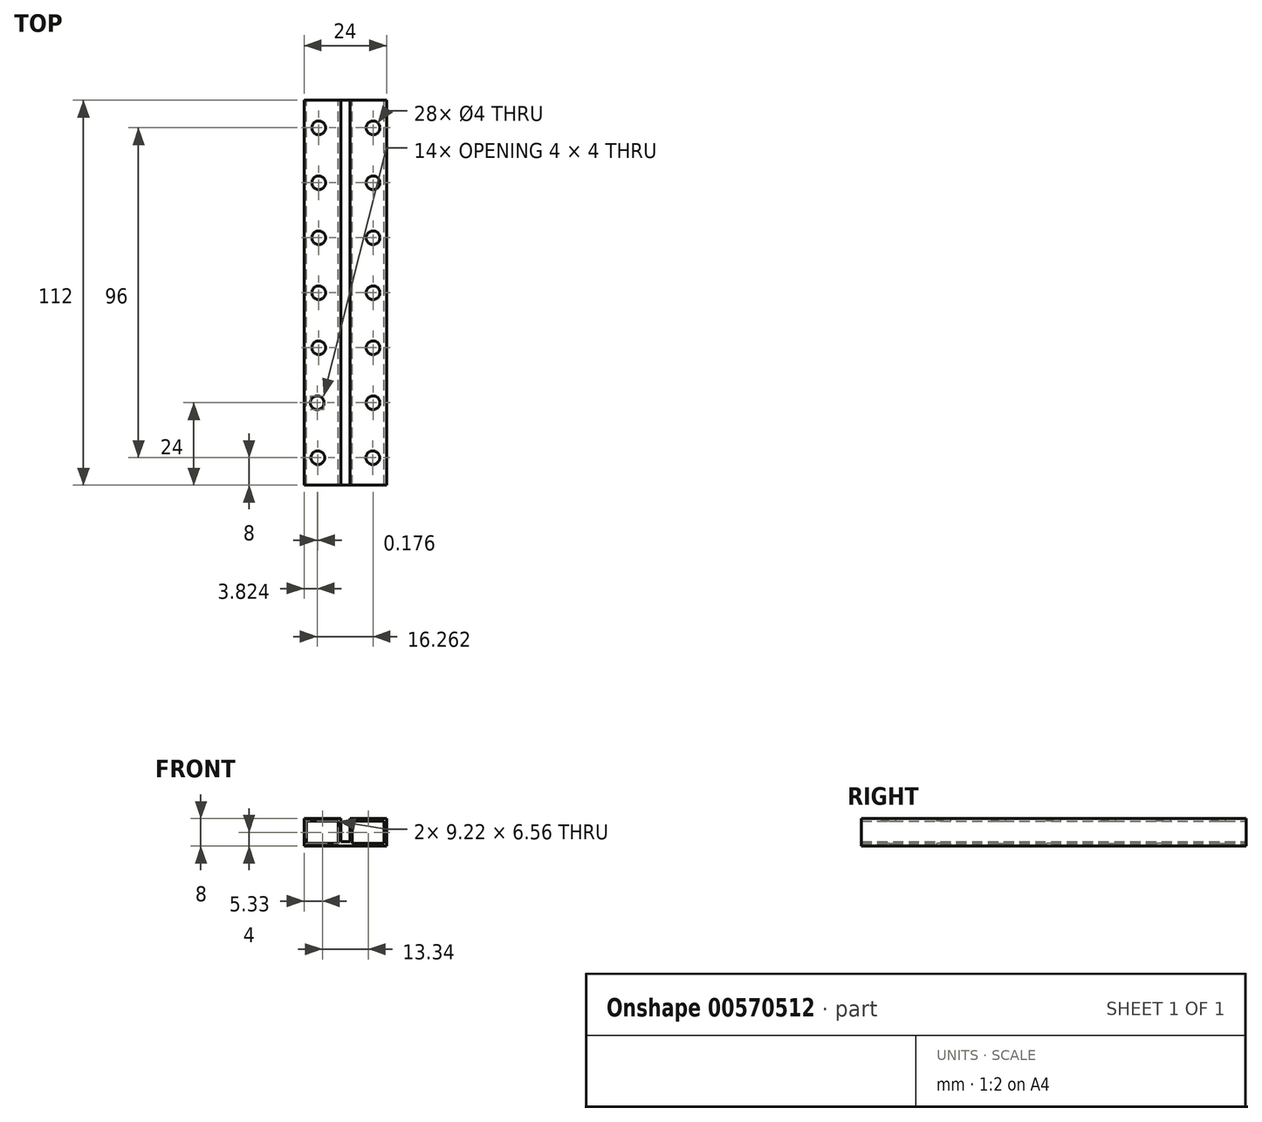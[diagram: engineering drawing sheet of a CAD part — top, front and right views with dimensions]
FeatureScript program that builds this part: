
annotation { "Feature Type Name" : "Feature", "Feature Type Description" : "" }
export const myFeature = defineFeature(function(context is Context, id is Id, definition is map)
    precondition{}
    {
        {
            var Q0;
            Q0=qCreatedBy(makeId("Front.planeOp"),FACE);
            var sketch = newSketch(context, id + "F0", { "sketchPlane" : qUnion([Q0])});
            skLineSegment(sketch, "E0.bottom", {"start": v(-12, 4) * mm, "end": v(12, 4) * mm});
            skLineSegment(sketch, "E0.top", {"start": v(-12, -4) * mm, "end": v(12, -4) * mm});
            skLineSegment(sketch, "E0.left", {"start": v(-12, 4) * mm, "end": v(-12, -4) * mm});
            skLineSegment(sketch, "E0.right", {"start": v(12, 4) * mm, "end": v(12, -4) * mm});
            skPoint(sketch, "E0.middle", {"position": v(0, 0) * mm});
            skLineSegment(sketch, "E1.bottom", {"start": v(-1.34, 10.75) * mm, "end": v(1.34, 10.75) * mm});
            skLineSegment(sketch, "E1.top", {"start": v(-1.34, -2.75) * mm, "end": v(1.34, -2.75) * mm});
            skLineSegment(sketch, "E1.left", {"start": v(-1.34, 10.75) * mm, "end": v(-1.34, -2.75) * mm});
            skLineSegment(sketch, "E1.right", {"start": v(1.34, 10.75) * mm, "end": v(1.34, -2.75) * mm});
            skPoint(sketch, "E1.middle", {"position": v(0, 4) * mm});
            skLineSegment(sketch, "E2.bottom", {"start": v(11.28, -3.28) * mm, "end": v(2.06, -3.28) * mm});
            skLineSegment(sketch, "E2.top", {"start": v(11.28, 3.28) * mm, "end": v(2.06, 3.28) * mm});
            skLineSegment(sketch, "E2.left", {"start": v(11.28, -3.28) * mm, "end": v(11.28, 3.28) * mm});
            skLineSegment(sketch, "E2.right", {"start": v(2.06, -3.28) * mm, "end": v(2.06, 3.28) * mm});
            skLineSegment(sketch, "E3.bottom", {"start": v(-2.06, 3.28) * mm, "end": v(-11.28, 3.28) * mm});
            skLineSegment(sketch, "E3.top", {"start": v(-2.06, -3.28) * mm, "end": v(-11.28, -3.28) * mm});
            skLineSegment(sketch, "E3.left", {"start": v(-2.06, 3.28) * mm, "end": v(-2.06, -3.28) * mm});
            skLineSegment(sketch, "E3.right", {"start": v(-11.28, 3.28) * mm, "end": v(-11.28, -3.28) * mm});
            skLineSegment(sketch, "E4.bottom", {"start": v(-9.78, 3.28) * mm, "end": v(-6.31, 3.28) * mm});
            skLineSegment(sketch, "E4.top", {"start": v(-9.78, -3.28) * mm, "end": v(-6.31, -3.28) * mm});
            skLineSegment(sketch, "E4.left", {"start": v(-9.78, 3.28) * mm, "end": v(-9.78, -3.28) * mm});
            skLineSegment(sketch, "E4.right", {"start": v(-6.31, 3.28) * mm, "end": v(-6.31, -3.28) * mm});
            skLineSegment(sketch, "E5.bottom", {"start": v(6.31, 3.28) * mm, "end": v(9.78, 3.28) * mm});
            skLineSegment(sketch, "E5.top", {"start": v(6.31, -3.28) * mm, "end": v(9.78, -3.28) * mm});
            skLineSegment(sketch, "E5.left", {"start": v(6.31, 3.28) * mm, "end": v(6.31, -3.28) * mm});
            skLineSegment(sketch, "E5.right", {"start": v(9.78, 3.28) * mm, "end": v(9.78, -3.28) * mm});
            skCircle(sketch, "E6", {"center": v(-8, 0) * mm, "radius": 2.16 * mm});
            skCircle(sketch, "E7", {"center": v(8, 0) * mm, "radius": 2.16 * mm});
            skSolve(sketch);
        }
        {
            var Q0;
            Q0=makeQuery(id+"F0.imprint","IMPRINT",FACE,{"disambiguationData":[TD([[makeQuery(id+"F0.imprint","IMPRINT",EDGE,{"derivedFrom":sQuery(id+"F0.wireOp",EDGE,"E0.top")}),1.0]])]});
            var Q1;
            {var subQ0=sQuery(id+"F0.wireOp",EDGE,"E4.bottom");Q1=makeQuery(id+"F0.imprint","IMPRINT",FACE,{"disambiguationData":[TD([[makeQuery(id+"F0.imprint","IMPRINT",EDGE,{"derivedFrom":subQ0}),-1.0]])]});}
            var Q2;
            {var subQ0=sQuery(id+"F0.wireOp",EDGE,"E4.top");Q2=makeQuery(id+"F0.imprint","IMPRINT",FACE,{"disambiguationData":[TD([[makeQuery(id+"F0.imprint","IMPRINT",EDGE,{"derivedFrom":subQ0}),1.0]])]});}
            var Q3;
            {var subQ0=sQuery(id+"F0.wireOp",EDGE,"E5.bottom");Q3=makeQuery(id+"F0.imprint","IMPRINT",FACE,{"disambiguationData":[TD([[makeQuery(id+"F0.imprint","IMPRINT",EDGE,{"derivedFrom":subQ0}),-1.0]])]});}
            var Q4;
            {var subQ0=sQuery(id+"F0.wireOp",EDGE,"E5.top");Q4=makeQuery(id+"F0.imprint","IMPRINT",FACE,{"disambiguationData":[TD([[makeQuery(id+"F0.imprint","IMPRINT",EDGE,{"derivedFrom":subQ0}),1.0]])]});}
            extrude(context, id + "F1", {"entities" : qUnion([Q0, Q1, Q2, Q3, Q4]), "depth" : 112 * mm, "offsetDistance" : 25 * mm});
        }
        {
            var Q0;
            {var subQ0=sQuery(id+"F0.wireOp",EDGE,"E0.bottom");Q0=makeQuery(id+"F1.opExtrude","SWEPT_FACE",FACE,{"disambiguationData":[OSD([subQ0]),TDD([makeQuery(id+"F0.imprint","IMPRINT",EDGE,{"disambiguationData":[TD([[makeQuery(id+"F0.imprint","INTERSECT",VERTEX,{"derivedFrom":[subQ0,sQuery(id+"F0.wireOp",EDGE,"E0.right")]}),1.0]])],"derivedFrom":subQ0})])]});}
            var sketch = newSketch(context, id + "F2", { "sketchPlane" : qUnion([Q0])});
            skCircle(sketch, "E8", {"center": v(8, -104) * mm, "radius": 2 * mm});
            skCircle(sketch, "E9", {"center": v(-8, -104) * mm, "radius": 2 * mm});
            skCircle(sketch, "E10", {"center": v(8.09, -88) * mm, "radius": 2 * mm});
            skCircle(sketch, "E11", {"center": v(-8.18, -88) * mm, "radius": 2 * mm});
            skCircle(sketch, "E12", {"center": v(8.09, -72) * mm, "radius": 2 * mm});
            skCircle(sketch, "E13", {"center": v(-7.73, -72) * mm, "radius": 2 * mm});
            skCircle(sketch, "E14", {"center": v(8.09, -56) * mm, "radius": 2 * mm});
            skCircle(sketch, "E15", {"center": v(-7.73, -56) * mm, "radius": 2 * mm});
            skCircle(sketch, "E16", {"center": v(8.09, -40) * mm, "radius": 2 * mm});
            skCircle(sketch, "E17", {"center": v(-7.73, -40) * mm, "radius": 2 * mm});
            skCircle(sketch, "E18", {"center": v(8.09, -24) * mm, "radius": 2 * mm});
            skCircle(sketch, "E19", {"center": v(-7.73, -24) * mm, "radius": 2 * mm});
            skCircle(sketch, "E20", {"center": v(8.09, -8) * mm, "radius": 2 * mm});
            skCircle(sketch, "E21", {"center": v(-7.73, -8) * mm, "radius": 2 * mm});
            skSolve(sketch);
        }
        {
            var Q0;
            Q0=makeQuery(id+"F2.imprint","IMPRINT",FACE,{"disambiguationData":[TD([[makeQuery(id+"F2.imprint","IMPRINT",EDGE,{"derivedFrom":sQuery(id+"F2.wireOp",EDGE,"E9")}),1.0]])]});
            var Q1;
            Q1=makeQuery(id+"F2.imprint","IMPRINT",FACE,{"disambiguationData":[TD([[makeQuery(id+"F2.imprint","IMPRINT",EDGE,{"derivedFrom":sQuery(id+"F2.wireOp",EDGE,"E8")}),1.0]])]});
            var Q2;
            Q2=makeQuery(id+"F2.imprint","IMPRINT",FACE,{"disambiguationData":[TD([[makeQuery(id+"F2.imprint","IMPRINT",EDGE,{"derivedFrom":sQuery(id+"F2.wireOp",EDGE,"E11")}),1.0]])]});
            var Q3;
            Q3=makeQuery(id+"F2.imprint","IMPRINT",FACE,{"disambiguationData":[TD([[makeQuery(id+"F2.imprint","IMPRINT",EDGE,{"derivedFrom":sQuery(id+"F2.wireOp",EDGE,"E10")}),1.0]])]});
            var Q4;
            Q4=makeQuery(id+"F2.imprint","IMPRINT",FACE,{"disambiguationData":[TD([[makeQuery(id+"F2.imprint","IMPRINT",EDGE,{"derivedFrom":sQuery(id+"F2.wireOp",EDGE,"E13")}),1.0]])]});
            var Q5;
            Q5=makeQuery(id+"F2.imprint","IMPRINT",FACE,{"disambiguationData":[TD([[makeQuery(id+"F2.imprint","IMPRINT",EDGE,{"derivedFrom":sQuery(id+"F2.wireOp",EDGE,"E12")}),1.0]])]});
            var Q6;
            Q6=makeQuery(id+"F2.imprint","IMPRINT",FACE,{"disambiguationData":[TD([[makeQuery(id+"F2.imprint","IMPRINT",EDGE,{"derivedFrom":sQuery(id+"F2.wireOp",EDGE,"E15")}),1.0]])]});
            var Q7;
            Q7=makeQuery(id+"F2.imprint","IMPRINT",FACE,{"disambiguationData":[TD([[makeQuery(id+"F2.imprint","IMPRINT",EDGE,{"derivedFrom":sQuery(id+"F2.wireOp",EDGE,"E14")}),1.0]])]});
            var Q8;
            Q8=makeQuery(id+"F2.imprint","IMPRINT",FACE,{"disambiguationData":[TD([[makeQuery(id+"F2.imprint","IMPRINT",EDGE,{"derivedFrom":sQuery(id+"F2.wireOp",EDGE,"E17")}),1.0]])]});
            var Q9;
            Q9=makeQuery(id+"F2.imprint","IMPRINT",FACE,{"disambiguationData":[TD([[makeQuery(id+"F2.imprint","IMPRINT",EDGE,{"derivedFrom":sQuery(id+"F2.wireOp",EDGE,"E16")}),1.0]])]});
            var Q10;
            Q10=makeQuery(id+"F2.imprint","IMPRINT",FACE,{"disambiguationData":[TD([[makeQuery(id+"F2.imprint","IMPRINT",EDGE,{"derivedFrom":sQuery(id+"F2.wireOp",EDGE,"E18")}),1.0]])]});
            var Q11;
            Q11=makeQuery(id+"F2.imprint","IMPRINT",FACE,{"disambiguationData":[TD([[makeQuery(id+"F2.imprint","IMPRINT",EDGE,{"derivedFrom":sQuery(id+"F2.wireOp",EDGE,"E19")}),1.0]])]});
            var Q12;
            Q12=makeQuery(id+"F2.imprint","IMPRINT",FACE,{"disambiguationData":[TD([[makeQuery(id+"F2.imprint","IMPRINT",EDGE,{"derivedFrom":sQuery(id+"F2.wireOp",EDGE,"E21")}),1.0]])]});
            var Q13;
            Q13=makeQuery(id+"F2.imprint","IMPRINT",FACE,{"disambiguationData":[TD([[makeQuery(id+"F2.imprint","IMPRINT",EDGE,{"derivedFrom":sQuery(id+"F2.wireOp",EDGE,"E20")}),1.0]])]});
            extrude(context, id + "F3", {"entities" : qUnion([Q0, Q1, Q2, Q3, Q4, Q5, Q6, Q7, Q8, Q9, Q10, Q11, Q12, Q13]), "operationType" : NewBodyOperationType.REMOVE, "oppositeDirection" : true, "depth" : 8.1 * mm, "offsetDistance" : 25 * mm});
        }
    });
